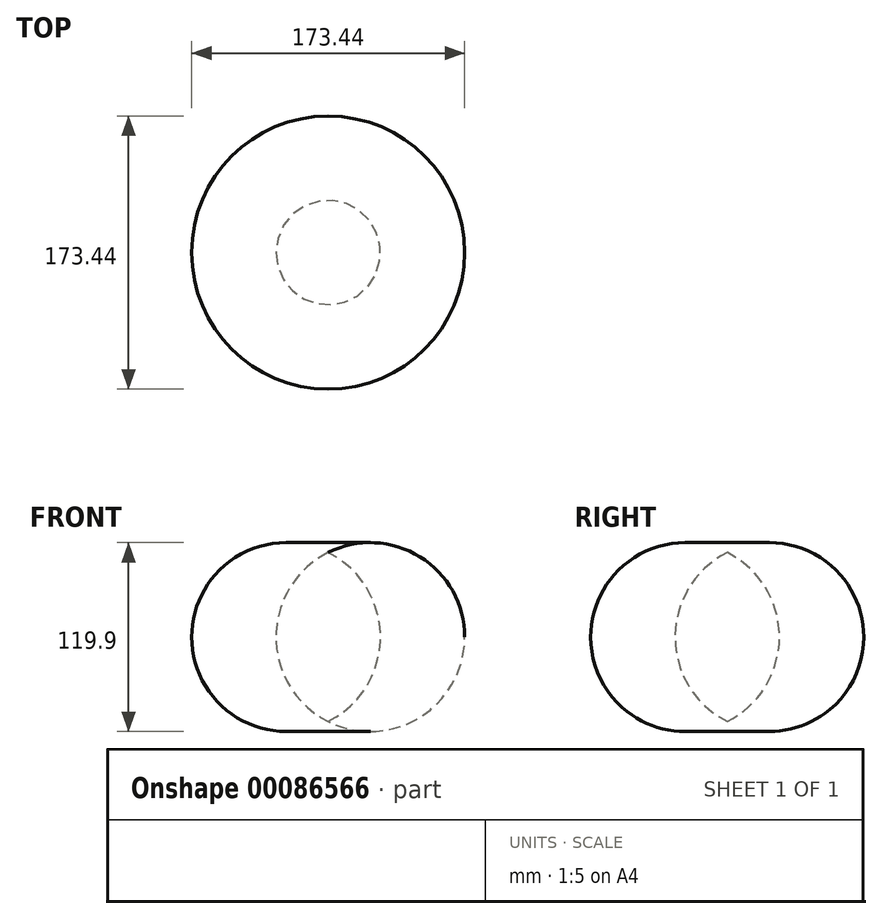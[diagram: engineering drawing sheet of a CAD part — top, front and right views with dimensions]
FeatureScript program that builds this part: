
annotation { "Feature Type Name" : "Feature", "Feature Type Description" : "" }
export const myFeature = defineFeature(function(context is Context, id is Id, definition is map)
    precondition{}
    {
        {
            var Q0;
            Q0=qCreatedBy(makeId("Front.planeOp"),FACE);
            var sketch = newSketch(context, id + "F0", { "sketchPlane" : qUnion([Q0])});
            skLineSegment(sketch, "E0", {"start": v(-54.53, 57.96) * mm, "end": v(-54.53, -49.32) * mm});
            skArc(sketch, "E1", {"start": v(-54.53, -49.32) * mm, "mid": v(32.19, 4.32) * mm, "end": v(-54.53, 57.96) * mm});
            skSolve(sketch);
        }
        {
            var Q0;
            Q0=makeQuery(id+"F0.imprint","IMPRINT",FACE,{"disambiguationData":[TD([[makeQuery(id+"F0.imprint","IMPRINT",EDGE,{"derivedFrom":sQuery(id+"F0.wireOp",EDGE,"E0")}),1.0]])]});
            var sketch = newSketch(context, id + "F1", { "sketchPlane" : qUnion([Q0])});
            skSolve(sketch);
        }
        {
            var Q0;
            Q0 = qSketchRegion(id + "F1", true);
            var Q1;
            Q1=makeQuery(id+"F0.imprint","IMPRINT",FACE,{"disambiguationData":[TD([[makeQuery(id+"F0.imprint","IMPRINT",EDGE,{"derivedFrom":sQuery(id+"F0.wireOp",EDGE,"E0")}),1.0]])]});
            var Q2;
            Q2=sQuery(id+"F0.wireOp",EDGE,"E0");
            revolve(context, id + "F2", {"entities" : qUnion([Q0, Q1]), "axis" : qUnion([Q2]), "revolveType" : RevolveType.FULL});
        }
    });
